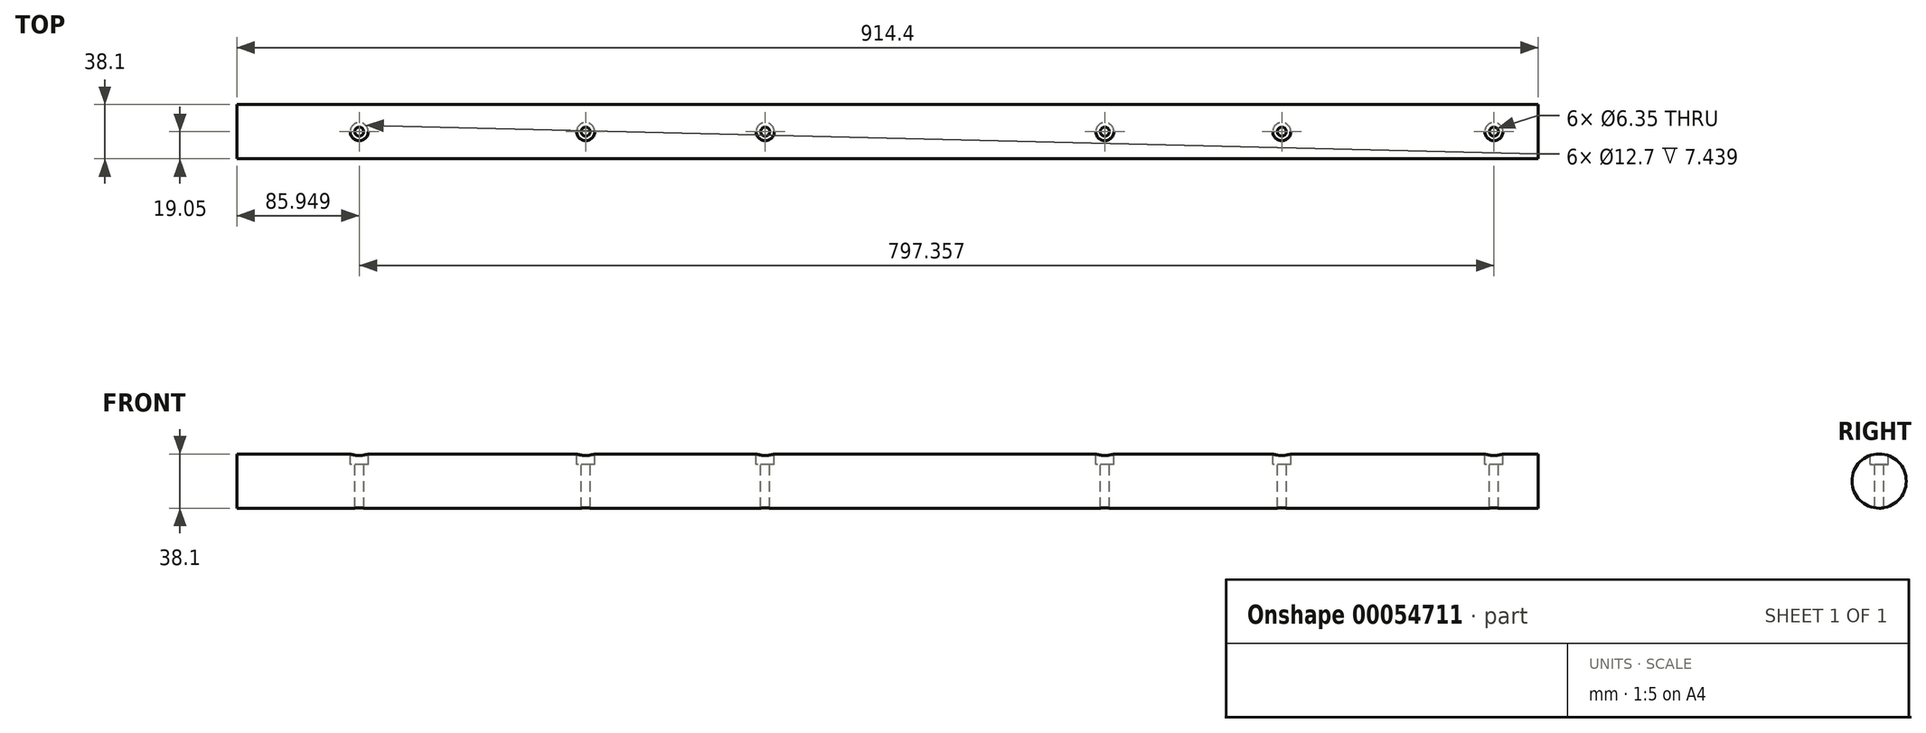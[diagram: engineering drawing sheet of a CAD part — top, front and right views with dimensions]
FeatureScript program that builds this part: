
annotation { "Feature Type Name" : "Feature", "Feature Type Description" : "" }
export const myFeature = defineFeature(function(context is Context, id is Id, definition is map)
    precondition{}
    {
        {
            var Q0;
            Q0=qCreatedBy(makeId("Front.planeOp"),FACE);
            var sketch = newSketch(context, id + "F0", { "sketchPlane" : qUnion([Q0])});
            skLineSegment(sketch, "E0.bottom", {"start": v(-497.22, 0) * mm, "end": v(417.18, 0) * mm});
            skLineSegment(sketch, "E0.top", {"start": v(-497.22, 19.05) * mm, "end": v(417.18, 19.05) * mm});
            skLineSegment(sketch, "E0.left", {"start": v(-497.22, 0) * mm, "end": v(-497.22, 19.05) * mm});
            skLineSegment(sketch, "E0.right", {"start": v(417.18, 0) * mm, "end": v(417.18, 19.05) * mm});
            skSolve(sketch);
        }
        {
            var Q0;
            Q0 = qSketchRegion(id + "F0", true);
            var Q1;
            Q1=sQuery(id+"F0.wireOp",EDGE,"E0.bottom");
            revolve(context, id + "F1", {"entities" : qUnion([Q0]), "axis" : qUnion([Q1]), "revolveType" : RevolveType.FULL});
        }
        {
            var Q0;
            Q0=qCreatedBy(makeId("Top.planeOp"),FACE);
            cPlane(context, id + "F2", {"entities" : qUnion([Q0]), "cplaneType" : CPlaneType.OFFSET, "offset" : 19.05 * mm, "width" : 152.4 * mm, "height" : 152.4 * mm});
        }
        {
            var Q0;
            Q0=qCreatedBy(id+"F2.planeOp",FACE);
            var sketch = newSketch(context, id + "F3", { "sketchPlane" : qUnion([Q0])});
            skPoint(sketch, "E1", {"position": v(-411.27, 0) * mm});
            skPoint(sketch, "E2", {"position": v(-252.17, 0) * mm});
            skPoint(sketch, "E3", {"position": v(-125.98, 0) * mm});
            skPoint(sketch, "E4", {"position": v(112.68, 0) * mm});
            skPoint(sketch, "E5", {"position": v(237.04, 0) * mm});
            skPoint(sketch, "E6", {"position": v(386.09, 0) * mm});
            skSolve(sketch);
        }
        {
            var Q0;
            Q0=sQuery(id+"F3.wireOp",VERTEX,"E2");
            var Q1;
            Q1=sQuery(id+"F3.wireOp",VERTEX,"E1");
            var Q2;
            Q2=sQuery(id+"F3.wireOp",VERTEX,"E3");
            var Q3;
            Q3=sQuery(id+"F3.wireOp",VERTEX,"E4");
            var Q4;
            Q4=sQuery(id+"F3.wireOp",VERTEX,"E5");
            var Q5;
            Q5=sQuery(id+"F3.wireOp",VERTEX,"E6");
            var Q6;
            Q6=makeQuery(id+"F1.opRevolve","SWEPT_BODY",BODY,{"disambiguationData":[OSD([sQuery(id+"F0.wireOp",EDGE,"E0.bottom"),sQuery(id+"F0.wireOp",EDGE,"E0.top"),sQuery(id+"F0.wireOp",EDGE,"E0.left"),sQuery(id+"F0.wireOp",EDGE,"E0.right")])]});
            hole(context, id + "F4", {"style" : HoleStyle.C_BORE, "holeDiameter" : 6.35 * mm, "cBoreDiameter" : 12.7 * mm, "cBoreDepth" : 6.35 * mm, "endStyle" : HoleEndStyle.THROUGH, "locations" : qUnion([Q0, Q1, Q2, Q3, Q4, Q5]), "scope" : qUnion([Q6])});
        }
    });
